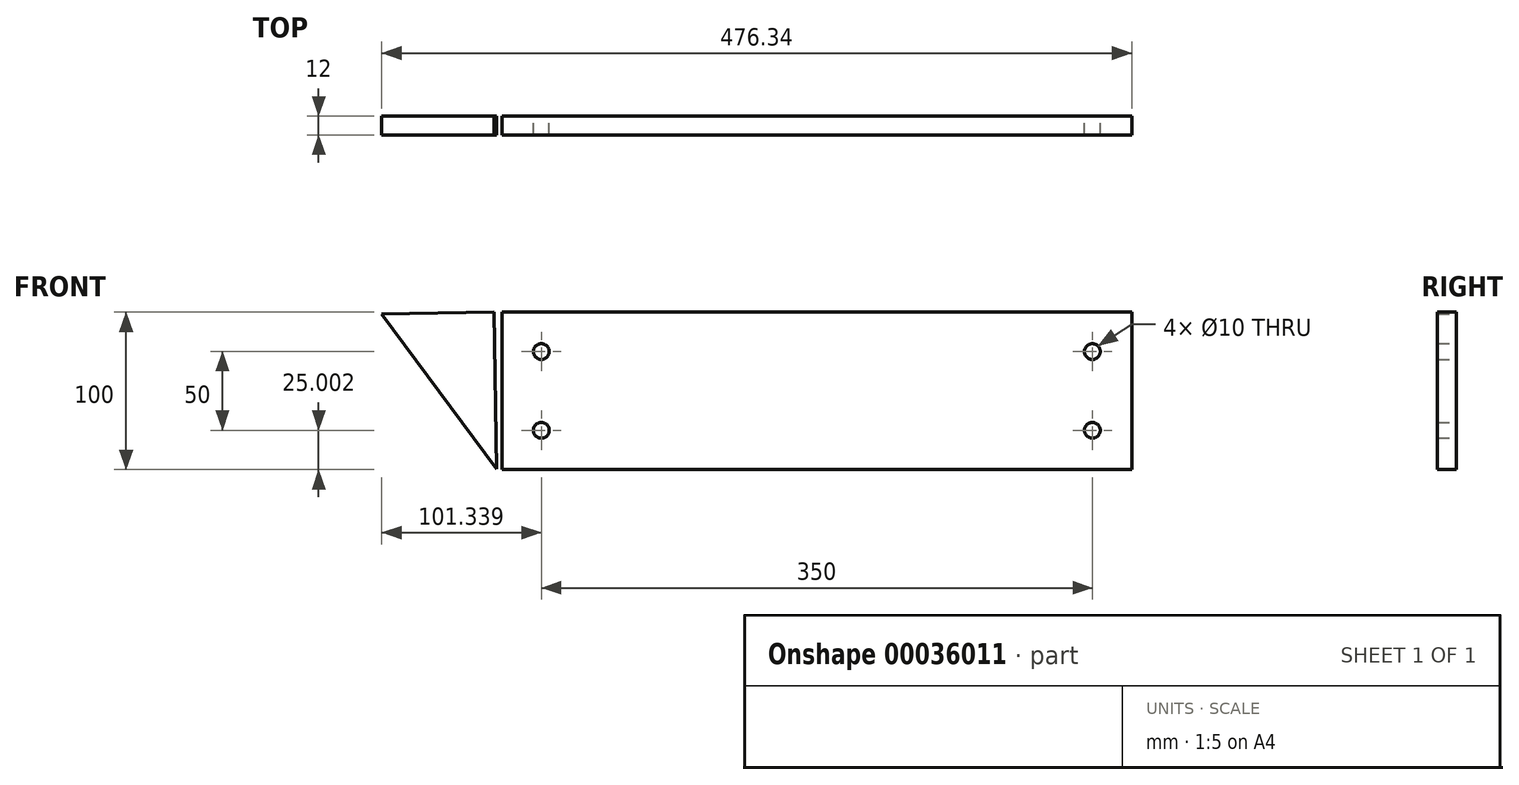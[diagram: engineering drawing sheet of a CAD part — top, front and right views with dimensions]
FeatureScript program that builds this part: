
annotation { "Feature Type Name" : "Feature", "Feature Type Description" : "" }
export const myFeature = defineFeature(function(context is Context, id is Id, definition is map)
    precondition{}
    {
        {
            var Q0;
            Q0=qCreatedBy(makeId("Front.planeOp"),FACE);
            var sketch = newSketch(context, id + "F0", { "sketchPlane" : qUnion([Q0])});
            skLineSegment(sketch, "E0.bottom", {"start": v(-167.3, 37.81) * mm, "end": v(232.7, 37.81) * mm});
            skLineSegment(sketch, "E0.top", {"start": v(-167.3, -62.19) * mm, "end": v(232.7, -62.19) * mm});
            skLineSegment(sketch, "E0.left", {"start": v(-167.3, 37.81) * mm, "end": v(-167.3, -62.19) * mm});
            skLineSegment(sketch, "E0.right", {"start": v(232.7, 37.81) * mm, "end": v(232.7, -62.19) * mm});
            skCircle(sketch, "E1", {"center": v(-142.3, 12.81) * mm, "radius": 5 * mm});
            skCircle(sketch, "E2", {"center": v(207.7, 12.81) * mm, "radius": 5 * mm});
            skCircle(sketch, "E3", {"center": v(207.7, -37.19) * mm, "radius": 5 * mm});
            skCircle(sketch, "E4", {"center": v(-142.3, -37.19) * mm, "radius": 5 * mm});
            skSolve(sketch);
        }
        {
            var Q0;
            Q0=makeQuery(id+"F0.imprint","IMPRINT",FACE,{"disambiguationData":[TD([[makeQuery(id+"F0.imprint","IMPRINT",EDGE,{"derivedFrom":sQuery(id+"F0.wireOp",EDGE,"E0.bottom")}),-1.0]])]});
            extrude(context, id + "F1", {"entities" : qUnion([Q0]), "depth" : 12 * mm});
        }
        {
            var Q0;
            Q0=qCreatedBy(makeId("Front.planeOp"),FACE);
            var sketch = newSketch(context, id + "F2", { "sketchPlane" : qUnion([Q0])});
            skLineSegment(sketch, "E5.bottom", {"start": v(-172.4, 37.8) * mm, "end": v(-243.64, 36.5) * mm});
            skLineSegment(sketch, "E5.left", {"start": v(-172.4, 37.8) * mm, "end": v(-170.59, -61.85) * mm});
            skLineSegment(sketch, "E6", {"start": v(-243.64, 36.5) * mm, "end": v(-170.59, -61.85) * mm});
            skLineSegment(sketch, "E7", {"start": v(-243.64, 36.5) * mm, "end": v(-172.4, 37.8) * mm});
            skSolve(sketch);
        }
        {
            var Q0;
            Q0=makeQuery(id+"F2.imprint","IMPRINT",FACE,{"disambiguationData":[TD([[makeQuery(id+"F2.imprint","IMPRINT",EDGE,{"derivedFrom":sQuery(id+"F2.wireOp",EDGE,"E6")}),1.0]])]});
            extrude(context, id + "F3", {"entities" : qUnion([Q0]), "depth" : 12 * mm});
        }
    });
